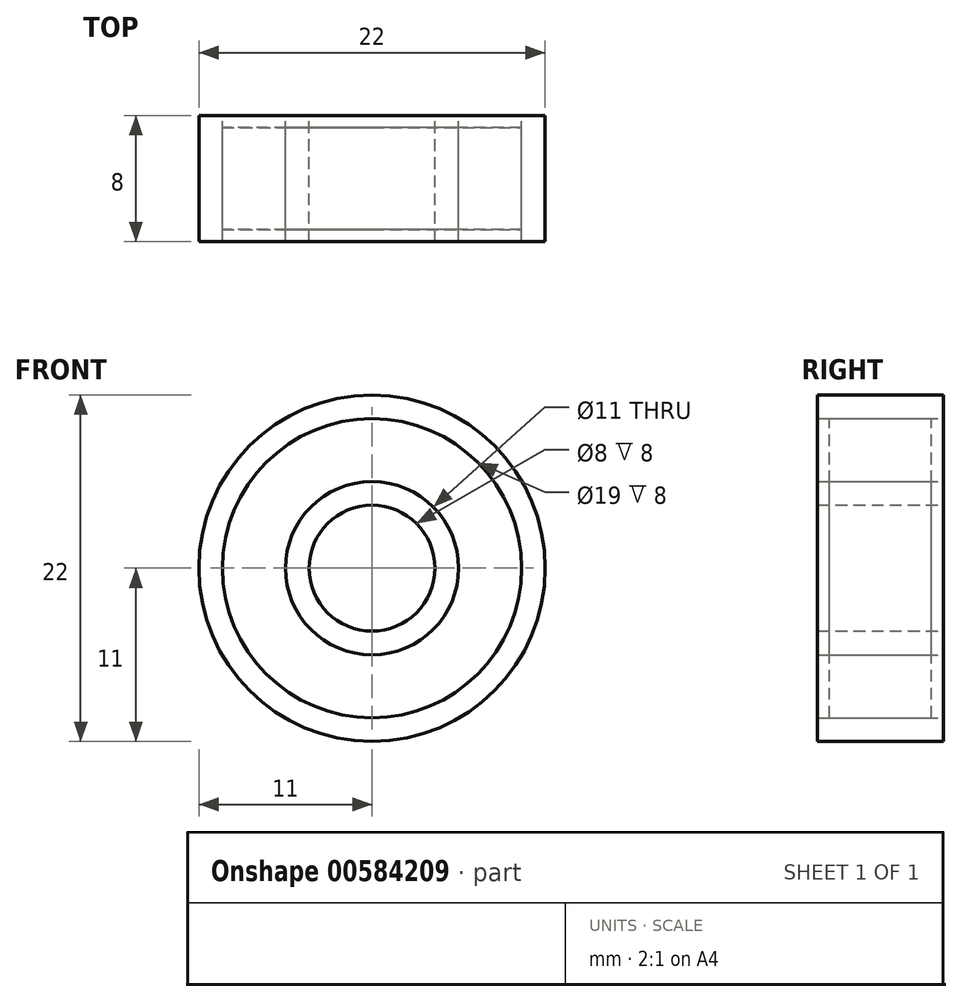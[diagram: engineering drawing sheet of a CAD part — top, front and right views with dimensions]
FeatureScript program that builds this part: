
annotation { "Feature Type Name" : "Feature", "Feature Type Description" : "" }
export const myFeature = defineFeature(function(context is Context, id is Id, definition is map)
    precondition{}
    {
        {
            var Q0;
            Q0=qCreatedBy(makeId("Front.planeOp"),FACE);
            var sketch = newSketch(context, id + "F0", { "sketchPlane" : qUnion([Q0])});
            skCircle(sketch, "E0", {"center": v(0, 0) * mm, "radius": 11 * mm});
            skCircle(sketch, "E1", {"center": v(0, 0) * mm, "radius": 9.5 * mm});
            skSolve(sketch);
        }
        {
            var Q0;
            Q0=makeQuery(id+"F0.imprint","IMPRINT",FACE,{"disambiguationData":[TD([[makeQuery(id+"F0.imprint","IMPRINT",EDGE,{"derivedFrom":sQuery(id+"F0.wireOp",EDGE,"E0")}),1.0]])]});
            extrude(context, id + "F1", {"entities" : qUnion([Q0]), "endBound" : BoundingType.SYMMETRIC, "depth" : 8 * mm, "offsetDistance" : 25.4 * mm});
        }
        {
            var Q0;
            Q0=qCreatedBy(makeId("Front.planeOp"),FACE);
            var sketch = newSketch(context, id + "F2", { "sketchPlane" : qUnion([Q0])});
            skCircle(sketch, "E2", {"center": v(0, 0) * mm, "radius": 4 * mm});
            skCircle(sketch, "E3", {"center": v(0, 0) * mm, "radius": 5.5 * mm});
            skSolve(sketch);
        }
        {
            var Q0;
            Q0=makeQuery(id+"F2.imprint","IMPRINT",FACE,{"disambiguationData":[TD([[makeQuery(id+"F2.imprint","IMPRINT",EDGE,{"derivedFrom":sQuery(id+"F2.wireOp",EDGE,"E2")}),-1.0]])]});
            extrude(context, id + "F3", {"entities" : qUnion([Q0]), "endBound" : BoundingType.SYMMETRIC, "depth" : 8 * mm, "offsetDistance" : 25.4 * mm});
        }
        {
            var Q0;
            Q0=qCreatedBy(makeId("Front.planeOp"),FACE);
            var sketch = newSketch(context, id + "F4", { "sketchPlane" : qUnion([Q0])});
            skCircle(sketch, "E4", {"center": v(0, 0) * mm, "radius": 9.5 * mm});
            skCircle(sketch, "E5", {"center": v(0, 0) * mm, "radius": 5.5 * mm});
            skSolve(sketch);
        }
        {
            var Q0;
            Q0=makeQuery(id+"F4.imprint","IMPRINT",FACE,{"disambiguationData":[TD([[makeQuery(id+"F4.imprint","IMPRINT",EDGE,{"derivedFrom":sQuery(id+"F4.wireOp",EDGE,"E4")}),1.0]])]});
            extrude(context, id + "F5", {"entities" : qUnion([Q0]), "endBound" : BoundingType.SYMMETRIC, "depth" : 6.5 * mm, "offsetDistance" : 25.4 * mm});
        }
    });
